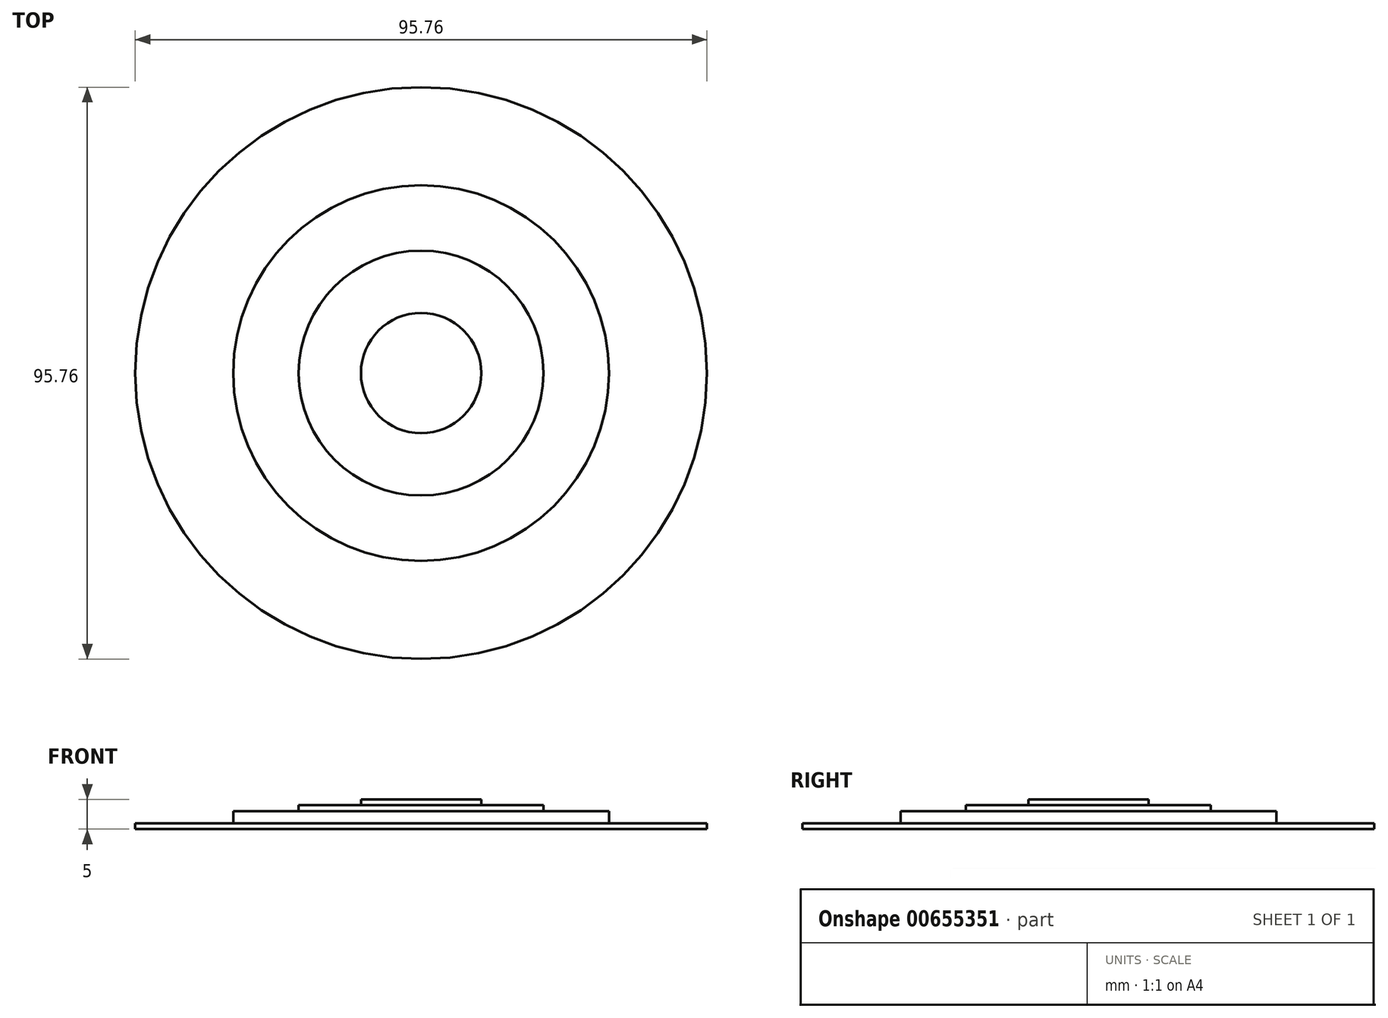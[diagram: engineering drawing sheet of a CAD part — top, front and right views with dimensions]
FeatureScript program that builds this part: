
annotation { "Feature Type Name" : "Feature", "Feature Type Description" : "" }
export const myFeature = defineFeature(function(context is Context, id is Id, definition is map)
    precondition{}
    {
        {
            var Q0;
            Q0=qCreatedBy(makeId("Top.planeOp"),FACE);
            var sketch = newSketch(context, id + "F0", { "sketchPlane" : qUnion([Q0])});
            skCircle(sketch, "E0", {"center": v(0, 0) * mm, "radius": 47.88 * mm});
            skSolve(sketch);
        }
        {
            var Q0;
            Q0 = qSketchRegion(id + "F0", true);
            extrude(context, id + "F1", {"entities" : qUnion([Q0]), "depth" : 1 * mm, "offsetDistance" : 25 * mm});
        }
        {
            var Q0;
            Q0=qCreatedBy(makeId("Top.planeOp"),FACE);
            var sketch = newSketch(context, id + "F2", { "sketchPlane" : qUnion([Q0])});
            skCircle(sketch, "E1", {"center": v(0, 0) * mm, "radius": 31.46 * mm});
            skSolve(sketch);
        }
        {
            var Q0;
            Q0 = qSketchRegion(id + "F2", true);
            extrude(context, id + "F3", {"entities" : qUnion([Q0]), "operationType" : NewBodyOperationType.ADD, "depth" : 3 * mm, "offsetDistance" : 25 * mm});
        }
        {
            var Q0;
            Q0=qCreatedBy(makeId("Top.planeOp"),FACE);
            var sketch = newSketch(context, id + "F4", { "sketchPlane" : qUnion([Q0])});
            skCircle(sketch, "E2", {"center": v(0, 0) * mm, "radius": 20.5 * mm});
            skSolve(sketch);
        }
        {
            var Q0;
            Q0 = qSketchRegion(id + "F4", true);
            extrude(context, id + "F5", {"entities" : qUnion([Q0]), "operationType" : NewBodyOperationType.ADD, "depth" : 4 * mm, "offsetDistance" : 25 * mm});
        }
        {
            var Q0;
            Q0=qCreatedBy(makeId("Top.planeOp"),FACE);
            var sketch = newSketch(context, id + "F6", { "sketchPlane" : qUnion([Q0])});
            skCircle(sketch, "E3", {"center": v(0, 0) * mm, "radius": 10.07 * mm});
            skSolve(sketch);
        }
        {
            var Q0;
            Q0 = qSketchRegion(id + "F6", true);
            extrude(context, id + "F7", {"entities" : qUnion([Q0]), "operationType" : NewBodyOperationType.ADD, "depth" : 5 * mm, "offsetDistance" : 25 * mm});
        }
    });
